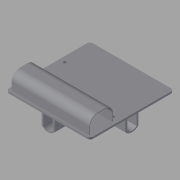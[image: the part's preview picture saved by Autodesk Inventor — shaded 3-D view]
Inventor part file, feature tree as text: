
AUTODESK INVENTOR PART (.ipt)
format: ipt  version: 2015 (Build 190159000, 159)  size: 174,080 bytes
history: native  units: in
note: dims shown in document units (in); Inventor stores cm internally (conversion verified against a paired STEP export)
features: extrude x5, sketch x5, fillet x2, plane x1, pattern_circular x1
ambient origin geometry x8: Origin, YZ Plane, XZ Plane, XY Plane, X Axis, Y Axis, Z Axis, Center Point
bodies: Solid1 (feature_tree)
feature tree (14):
  extrude  "Extrusion1"  Depth=0.1969in
  fillet  "Fillet1"  Radius=0.1969in
  fillet  "Fillet2"  [1 undecoded]
  plane  "Work Plane1"
  extrude  "Extrusion2"  Depth=0.4921in
  extrude  "Extrusion3"  Depth=5.1181in TaperAngle=0.0deg
  pattern_circular  "Circular Pattern1"  [2 undecoded]
  extrude  "Extrusion5"  Depth=0.7087in TaperAngle=0.0deg
  extrude  "Extrusion6"  Depth=0.1181in TaperAngle=360.0deg
  sketch  "Sketch1"  dims[d4=0.1181in d5=0.0in d6=0.1969in d7=0.1969in d8=-0.1969in]
  sketch  "Sketch5"  dims[d9=0.4921in d11=0.4921in]
  sketch  "Sketch6"  dims[d12=0.0394in d13=5.1181in d14=0.0in]
  sketch  "Sketch8"  dims[d17=0.7087in]
  sketch  "Sketch9"  dims[d21=0.1181in d22=0.1181in d24=0.7087in d25=0.0in d26=1.5748in d27=360.0deg d35=0.1969in d36=0.1181in d37=0.0in d39=0.1969in d40=0.1181in d41=0.0in]
note: 3 required parameter values undecoded (feature->parameter linkage not recoverable at this tier; creation-order binding heuristic only, values carry confidence <= 0.55)
